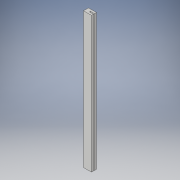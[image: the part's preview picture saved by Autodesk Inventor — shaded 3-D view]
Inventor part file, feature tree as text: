
AUTODESK INVENTOR PART (.ipt)
format: ipt  version: 2017 (Build 210142000, 142)  size: 102,400 bytes
history: native  units: in
note: dims shown in document units (in); Inventor stores cm internally (conversion verified against a paired STEP export)
features: extrude x1, sketch x1
ambient origin geometry x8: Origin, YZ Plane, XZ Plane, XY Plane, X Axis, Y Axis, Z Axis, Center Point
bodies: Solid1 (feature_tree)
feature tree (2):
  extrude  "Extrusion1"  Depth=0.25in
  sketch  "Sketch1"  dims[d0=1.0in d1=0.25in d2=0.5in d3=0.125in d4=1.0in d5=0.25in d6=17.0in d7=0.0in]
